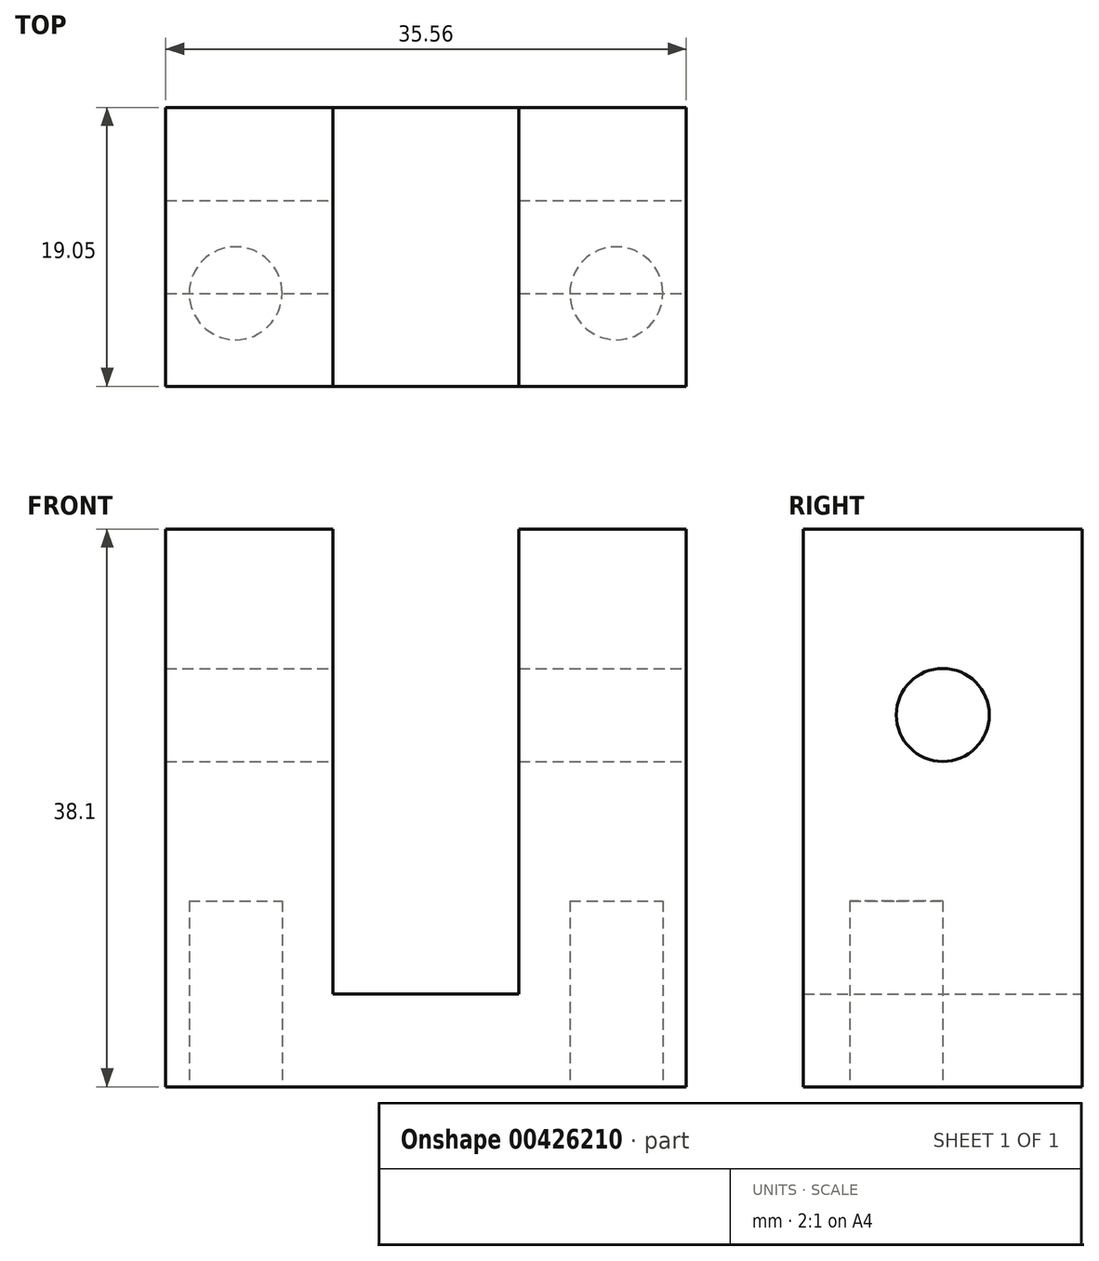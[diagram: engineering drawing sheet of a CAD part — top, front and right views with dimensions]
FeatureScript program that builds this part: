
annotation { "Feature Type Name" : "Feature", "Feature Type Description" : "" }
export const myFeature = defineFeature(function(context is Context, id is Id, definition is map)
    precondition{}
    {
        {
            var Q0;
            Q0=qCreatedBy(makeId("Front.planeOp"),FACE);
            var sketch = newSketch(context, id + "F0", { "sketchPlane" : qUnion([Q0])});
            skLineSegment(sketch, "E0.bottom", {"start": v(0, 0) * mm, "end": v(11.43, 0) * mm});
            skLineSegment(sketch, "E0.top", {"start": v(0, 38.1) * mm, "end": v(11.43, 38.1) * mm});
            skLineSegment(sketch, "E0.left", {"start": v(0, 0) * mm, "end": v(0, 38.1) * mm});
            skLineSegment(sketch, "E0.right", {"start": v(11.43, 0) * mm, "end": v(11.43, 38.1) * mm});
            skLineSegment(sketch, "E1.bottom", {"start": v(11.43, 0) * mm, "end": v(24.13, 0) * mm});
            skLineSegment(sketch, "E1.top", {"start": v(11.43, 6.35) * mm, "end": v(24.13, 6.35) * mm});
            skLineSegment(sketch, "E1.left", {"start": v(11.43, 0) * mm, "end": v(11.43, 6.35) * mm});
            skLineSegment(sketch, "E1.right", {"start": v(24.13, 0) * mm, "end": v(24.13, 6.35) * mm});
            skLineSegment(sketch, "E2.bottom", {"start": v(24.13, 0) * mm, "end": v(35.56, 0) * mm});
            skLineSegment(sketch, "E2.top", {"start": v(24.13, 38.1) * mm, "end": v(35.56, 38.1) * mm});
            skLineSegment(sketch, "E2.left", {"start": v(24.13, 0) * mm, "end": v(24.13, 38.1) * mm});
            skLineSegment(sketch, "E2.right", {"start": v(35.56, 0) * mm, "end": v(35.56, 38.1) * mm});
            skLineSegment(sketch, "E3", {"start": v(-3.8, 25.4) * mm, "end": v(7.77, 25.4) * mm, "construction": true});
            skSolve(sketch);
        }
        {
            var Q0;
            Q0 = qSketchRegion(id + "F0", true);
            extrude(context, id + "F1", {"entities" : qUnion([Q0]), "depth" : 19.05 * mm});
        }
        {
            var Q0;
            Q0=makeQuery(id+"F1.opExtrude","SWEPT_FACE",FACE,{"disambiguationData":[OSD([sQuery(id+"F0.wireOp",EDGE,"E2.right")])]});
            var sketch = newSketch(context, id + "F2", { "sketchPlane" : qUnion([Q0])});
            skCircle(sketch, "E4", {"center": v(-9.53, 25.4) * mm, "radius": 3.18 * mm});
            skPoint(sketch, "E4.centerSnap0", {"position": v(-9.53, 38.1) * mm});
            skSolve(sketch);
        }
        {
            var Q0;
            Q0 = qSketchRegion(id + "F2", true);
            extrude(context, id + "F3", {"entities" : qUnion([Q0]), "operationType" : NewBodyOperationType.REMOVE, "endBound" : BoundingType.THROUGH_ALL, "oppositeDirection" : true, "depth" : 25.4 * mm});
        }
        {
            var Q0;
            Q0=makeQuery(id+"F1.opExtrude","SWEPT_FACE",FACE,{"disambiguationData":[OSD([sQuery(id+"F0.wireOp",EDGE,"E0.bottom"),sQuery(id+"F0.wireOp",EDGE,"E1.bottom"),sQuery(id+"F0.wireOp",EDGE,"E2.bottom")])]});
            var sketch = newSketch(context, id + "F4", { "sketchPlane" : qUnion([Q0])});
            skCircle(sketch, "E5", {"center": v(4.78, 12.7) * mm, "radius": 3.18 * mm});
            skCircle(sketch, "E6", {"center": v(30.78, 12.7) * mm, "radius": 3.18 * mm});
            skSolve(sketch);
        }
        {
            var Q0;
            Q0 = qSketchRegion(id + "F4", true);
            extrude(context, id + "F5", {"entities" : qUnion([Q0]), "operationType" : NewBodyOperationType.REMOVE, "oppositeDirection" : true, "depth" : 12.7 * mm});
        }
    });
